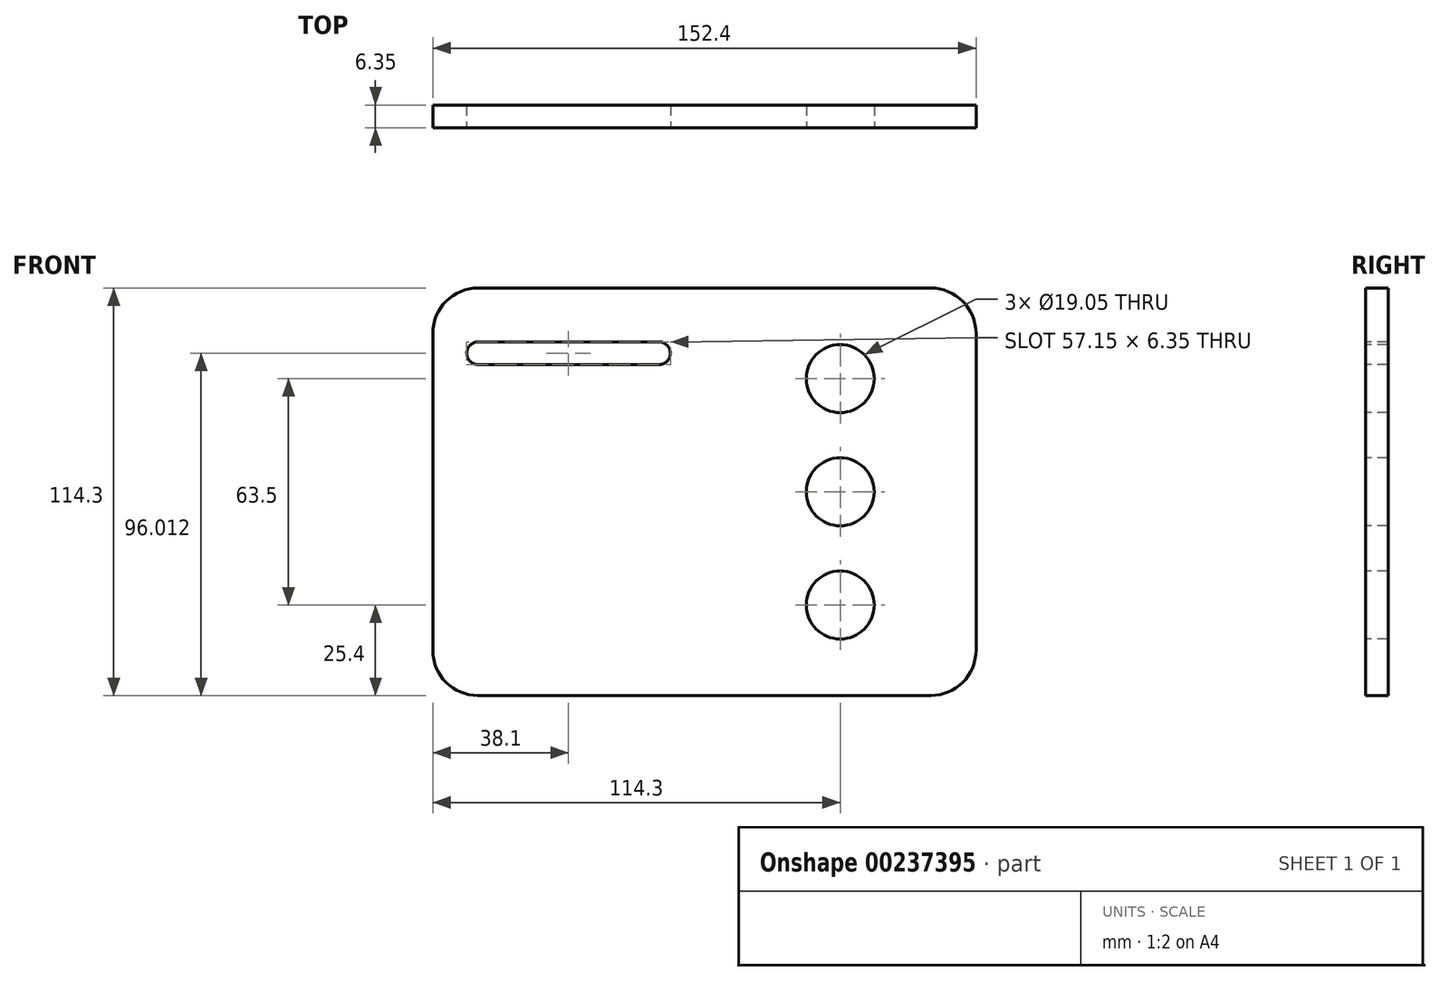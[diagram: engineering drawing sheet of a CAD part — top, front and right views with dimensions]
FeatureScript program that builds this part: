
annotation { "Feature Type Name" : "Feature", "Feature Type Description" : "" }
export const myFeature = defineFeature(function(context is Context, id is Id, definition is map)
    precondition{}
    {
        {
            var Q0;
            Q0=qCreatedBy(makeId("Front.planeOp"),FACE);
            var sketch = newSketch(context, id + "F0", { "sketchPlane" : qUnion([Q0])});
            skLineSegment(sketch, "E0.bottom", {"start": v(63.5, 57.15) * mm, "end": v(-63.5, 57.15) * mm});
            skLineSegment(sketch, "E0.top", {"start": v(63.5, -57.15) * mm, "end": v(-63.5, -57.15) * mm});
            skLineSegment(sketch, "E0.left", {"start": v(76.2, 44.45) * mm, "end": v(76.2, -44.45) * mm});
            skLineSegment(sketch, "E0.right", {"start": v(-76.2, 44.45) * mm, "end": v(-76.2, -44.45) * mm});
            skPoint(sketch, "E0.middle", {"position": v(0, 0) * mm});
            skPoint(sketch, "E1.visualSharp", {"position": v(-76.2, 57.15) * mm});
            skArc(sketch, "E1.filletArc", {"start": v(-63.5, 57.15) * mm, "mid": v(-72.48, 53.43) * mm, "end": v(-76.2, 44.45) * mm});
            skPoint(sketch, "E2.visualSharp", {"position": v(-76.2, -57.15) * mm});
            skArc(sketch, "E2.filletArc", {"start": v(-76.2, -44.45) * mm, "mid": v(-72.48, -53.43) * mm, "end": v(-63.5, -57.15) * mm});
            skPoint(sketch, "E3.visualSharp", {"position": v(76.2, -57.15) * mm});
            skArc(sketch, "E3.filletArc", {"start": v(63.5, -57.15) * mm, "mid": v(72.48, -53.43) * mm, "end": v(76.2, -44.45) * mm});
            skPoint(sketch, "E4.visualSharp", {"position": v(76.2, 57.15) * mm});
            skArc(sketch, "E4.filletArc", {"start": v(76.2, 44.45) * mm, "mid": v(72.48, 53.43) * mm, "end": v(63.5, 57.15) * mm});
            skSolve(sketch);
        }
        {
            var Q0;
            Q0 = qSketchRegion(id + "F0", true);
            extrude(context, id + "F1", {"entities" : qUnion([Q0]), "depth" : 6.35 * mm});
        }
        {
            var Q0;
            Q0=makeQuery(id+"F1.opExtrude","CAP_FACE",FACE,{"disambiguationData":[OSD([sQuery(id+"F0.wireOp",EDGE,"E0.bottom"),sQuery(id+"F0.wireOp",EDGE,"E0.top"),sQuery(id+"F0.wireOp",EDGE,"E0.left"),sQuery(id+"F0.wireOp",EDGE,"E0.right"),sQuery(id+"F0.wireOp",EDGE,"E1.filletArc"),sQuery(id+"F0.wireOp",EDGE,"E2.filletArc"),sQuery(id+"F0.wireOp",EDGE,"E3.filletArc"),sQuery(id+"F0.wireOp",EDGE,"E4.filletArc")])],"isStart":false});
            var sketch = newSketch(context, id + "F2", { "sketchPlane" : qUnion([Q0])});
            skPoint(sketch, "E5", {"position": v(38.1, 31.75) * mm});
            skPoint(sketch, "E6", {"position": v(38.1, 0) * mm});
            skPoint(sketch, "E7", {"position": v(38.1, -31.75) * mm});
            skSolve(sketch);
        }
        {
            var Q0;
            Q0=sQuery(id+"F2.wireOp",VERTEX,"E5");
            var Q1;
            Q1=sQuery(id+"F2.wireOp",VERTEX,"E6");
            var Q2;
            Q2=sQuery(id+"F2.wireOp",VERTEX,"E7");
            var Q3;
            Q3=makeQuery(id+"F1.opExtrude","SWEPT_BODY",BODY,{"disambiguationData":[OSD([sQuery(id+"F0.wireOp",EDGE,"E0.bottom"),sQuery(id+"F0.wireOp",EDGE,"E0.top"),sQuery(id+"F0.wireOp",EDGE,"E0.left"),sQuery(id+"F0.wireOp",EDGE,"E0.right"),sQuery(id+"F0.wireOp",EDGE,"E1.filletArc"),sQuery(id+"F0.wireOp",EDGE,"E2.filletArc"),sQuery(id+"F0.wireOp",EDGE,"E3.filletArc"),sQuery(id+"F0.wireOp",EDGE,"E4.filletArc")])]});
            hole(context, id + "F3", {"style" : HoleStyle.SIMPLE, "endStyle" : HoleEndStyle.THROUGH, "holeDiameter" : 19.05 * mm, "locations" : qUnion([Q0, Q1, Q2]), "scope" : qUnion([Q3]), "isTappedThrough" : true});
        }
        {
            var Q0;
            Q0=makeQuery(id+"F1.opExtrude","CAP_FACE",FACE,{"disambiguationData":[OSD([sQuery(id+"F0.wireOp",EDGE,"E0.bottom"),sQuery(id+"F0.wireOp",EDGE,"E0.top"),sQuery(id+"F0.wireOp",EDGE,"E0.left"),sQuery(id+"F0.wireOp",EDGE,"E0.right"),sQuery(id+"F0.wireOp",EDGE,"E1.filletArc"),sQuery(id+"F0.wireOp",EDGE,"E2.filletArc"),sQuery(id+"F0.wireOp",EDGE,"E3.filletArc"),sQuery(id+"F0.wireOp",EDGE,"E4.filletArc")])],"isStart":false});
            var sketch = newSketch(context, id + "F4", { "sketchPlane" : qUnion([Q0])});
            skLineSegment(sketch, "E8.bottom", {"start": v(-63.5, 42.04) * mm, "end": v(-12.7, 42.04) * mm});
            skLineSegment(sketch, "E8.top", {"start": v(-63.5, 35.69) * mm, "end": v(-12.7, 35.69) * mm});
            skArc(sketch, "E9", {"start": v(-63.5, 42.04) * mm, "mid": v(-66.67, 38.86) * mm, "end": v(-63.5, 35.69) * mm});
            skArc(sketch, "E10", {"start": v(-12.7, 35.69) * mm, "mid": v(-9.52, 38.86) * mm, "end": v(-12.7, 42.04) * mm});
            skSolve(sketch);
        }
        {
            var Q0;
            Q0 = qSketchRegion(id + "F4", true);
            extrude(context, id + "F5", {"entities" : qUnion([Q0]), "operationType" : NewBodyOperationType.REMOVE, "endBound" : BoundingType.THROUGH_ALL, "oppositeDirection" : true, "depth" : 25.4 * mm});
        }
    });
